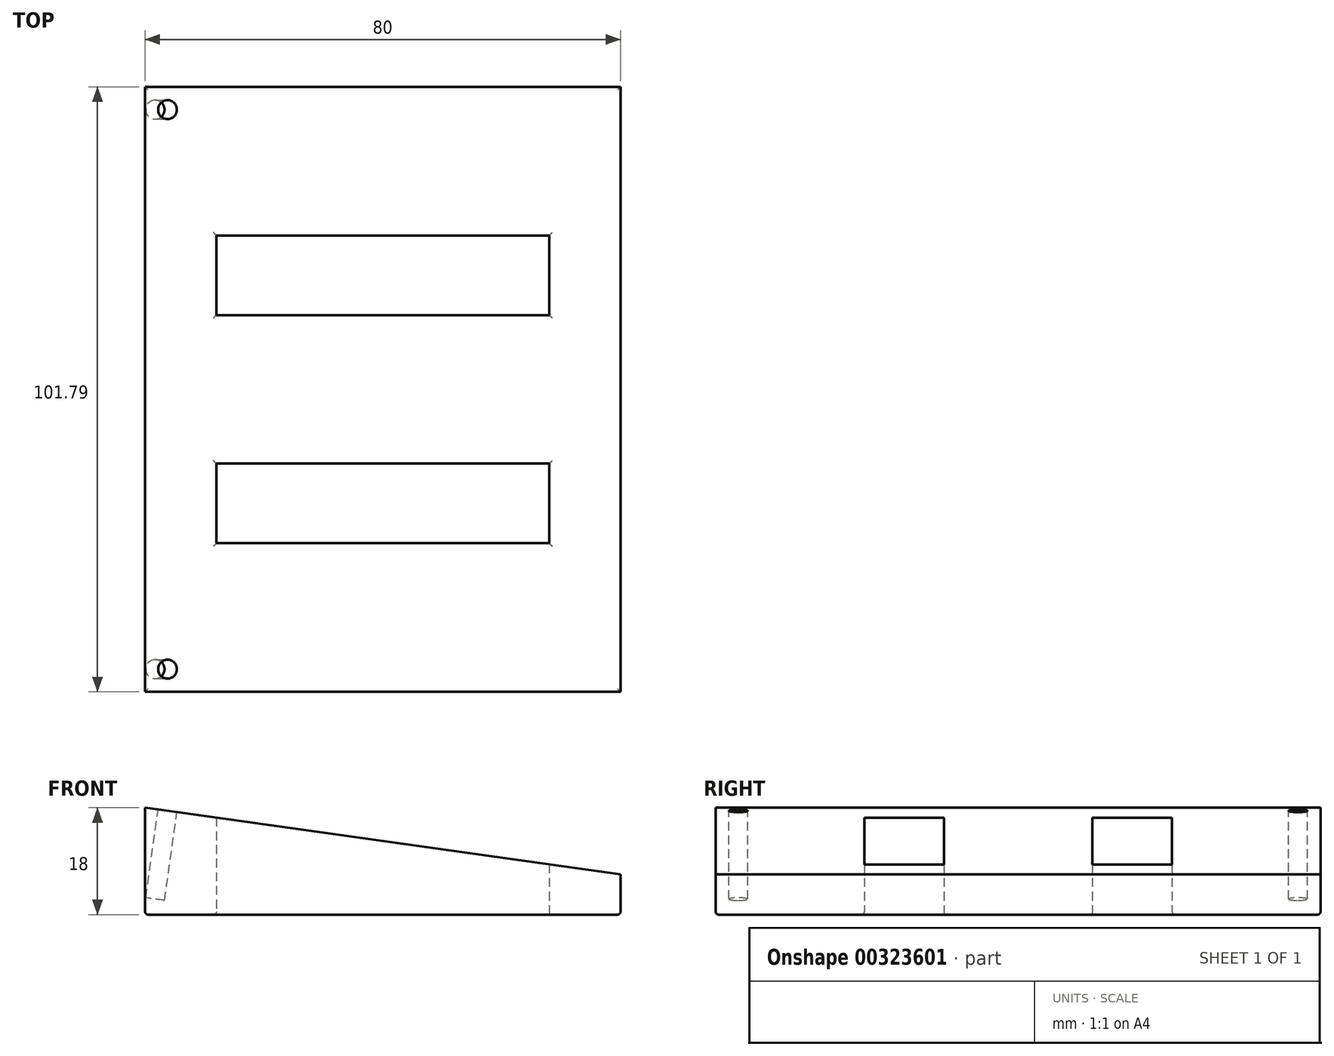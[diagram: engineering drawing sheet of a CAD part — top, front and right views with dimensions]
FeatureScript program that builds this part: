
annotation { "Feature Type Name" : "Feature", "Feature Type Description" : "" }
export const myFeature = defineFeature(function(context is Context, id is Id, definition is map)
    precondition{}
    {
        {
            var Q0;
            Q0=qCreatedBy(makeId("Front.planeOp"),FACE);
            var sketch = newSketch(context, id + "F0", { "sketchPlane" : qUnion([Q0])});
            skLineSegment(sketch, "E0", {"start": v(0, 0) * mm, "end": v(0, 6.76) * mm});
            skLineSegment(sketch, "E1", {"start": v(0, 6.76) * mm, "end": v(-80, 18) * mm});
            skLineSegment(sketch, "E2", {"start": v(-80, 18) * mm, "end": v(-80, 0) * mm});
            skLineSegment(sketch, "E3", {"start": v(-80, 0) * mm, "end": v(0, 0) * mm});
            skSolve(sketch);
        }
        {
            var Q0;
            Q0 = qSketchRegion(id + "F0", true);
            extrude(context, id + "F1", {"entities" : qUnion([Q0]), "depth" : 101.8 * mm, "offsetDistance" : 25 * mm});
        }
        {
            var Q0;
            Q0=makeQuery(id+"F1.opExtrude","SWEPT_FACE",FACE,{"disambiguationData":[OSD([sQuery(id+"F0.wireOp",EDGE,"E3")])]});
            var sketch = newSketch(context, id + "F2", { "sketchPlane" : qUnion([Q0])});
            skLineSegment(sketch, "E4.bottom", {"start": v(-68, 76.79) * mm, "end": v(-12, 76.79) * mm});
            skLineSegment(sketch, "E4.top", {"start": v(-68, 63.4) * mm, "end": v(-12, 63.4) * mm});
            skLineSegment(sketch, "E4.left", {"start": v(-68, 76.79) * mm, "end": v(-68, 63.4) * mm});
            skLineSegment(sketch, "E4.right", {"start": v(-12, 76.79) * mm, "end": v(-12, 63.4) * mm});
            skLineSegment(sketch, "E5.bottom", {"start": v(-12, 38.4) * mm, "end": v(-68, 38.4) * mm});
            skLineSegment(sketch, "E5.top", {"start": v(-12, 25) * mm, "end": v(-68, 25) * mm});
            skLineSegment(sketch, "E5.left", {"start": v(-12, 38.4) * mm, "end": v(-12, 25) * mm});
            skLineSegment(sketch, "E5.right", {"start": v(-68, 38.4) * mm, "end": v(-68, 25) * mm});
            skSolve(sketch);
        }
        {
            var Q0;
            Q0 = qSketchRegion(id + "F2", true);
            extrude(context, id + "F3", {"entities" : qUnion([Q0]), "operationType" : NewBodyOperationType.REMOVE, "oppositeDirection" : true, "depth" : 25 * mm, "offsetDistance" : 25 * mm});
        }
        {
            var Q0;
            Q0=makeQuery(id+"F1.opExtrude","SWEPT_FACE",FACE,{"disambiguationData":[OSD([sQuery(id+"F0.wireOp",EDGE,"E1")])]});
            var sketch = newSketch(context, id + "F4", { "sketchPlane" : qUnion([Q0])});
            skCircle(sketch, "E6", {"center": v(-77.92, -3.81) * mm, "radius": 1.6 * mm});
            skCircle(sketch, "E7", {"center": v(-77.92, -97.98) * mm, "radius": 1.6 * mm});
            skSolve(sketch);
        }
        {
            var Q0;
            Q0 = qSketchRegion(id + "F4", true);
            extrude(context, id + "F5", {"entities" : qUnion([Q0]), "operationType" : NewBodyOperationType.REMOVE, "oppositeDirection" : true, "depth" : 15 * mm, "offsetDistance" : 25 * mm});
        }
        {
            var Q0;
            Q0=makeQuery(id+"F5.boolean.opBoolean","COPY",EDGE,{"derivedFrom":makeQuery(id+"F5.opExtrude","CAP_EDGE",EDGE,{"disambiguationData":[OSD([sQuery(id+"F4.wireOp",EDGE,"E7")])],"isStart":true})});
            var Q1;
            Q1=makeQuery(id+"F5.boolean.opBoolean","COPY",EDGE,{"derivedFrom":makeQuery(id+"F5.opExtrude","CAP_EDGE",EDGE,{"disambiguationData":[OSD([sQuery(id+"F4.wireOp",EDGE,"E6")])],"isStart":true})});
            var Q2;
            Q2=makeQuery(id+"F1.opExtrude","SWEPT_FACE",FACE,{"disambiguationData":[OSD([sQuery(id+"F0.wireOp",EDGE,"E3")])]});
            fillet(context, id + "F6", {"entities" : qUnion([Q0, Q1, Q2]), "radius" : .5 * mm, "tangentPropagation" : true, "allowEdgeOverflow" : false});
        }
    });
